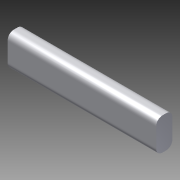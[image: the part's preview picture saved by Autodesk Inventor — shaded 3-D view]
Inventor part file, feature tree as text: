
AUTODESK INVENTOR PART (.ipt)
format: ipt  version: 2012 (Build 160160000, 160)  size: 92,160 bytes
history: native  units: mm
features: fillet x2, extrude x1, sketch x1
ambient origin geometry x8: Origin, YZ Plane, XZ Plane, XY Plane, X Axis, Y Axis, Z Axis, Center Point
bodies: Solid1 (feature_tree)
feature tree (4):
  extrude  "Extrusion1"  Depth=23.0mm
  fillet  "Fillet1"  Radius=46.0mm
  fillet  "Fillet2"  Radius=10.0mm
  sketch  "Sketch1"  dims[d0=212.0mm d1=23.0mm d2=46.0mm d3=0.0mm d4=10.0mm d5=10.0mm]
